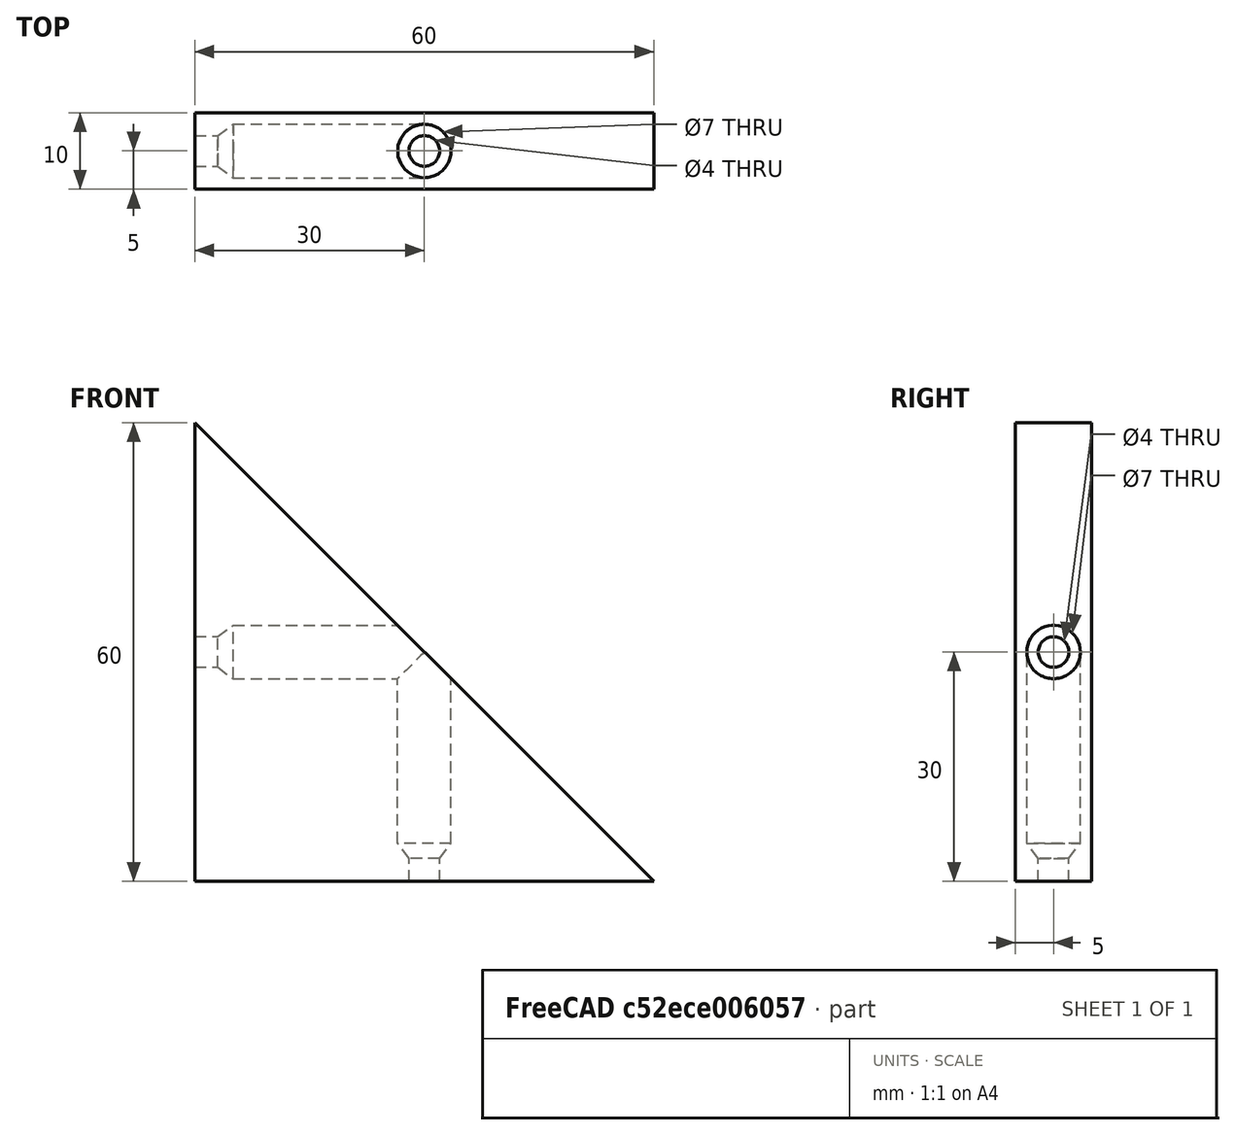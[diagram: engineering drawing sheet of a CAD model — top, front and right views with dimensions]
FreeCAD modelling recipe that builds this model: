
FCSTD DOCUMENT  (FreeCAD 0.16R6703 (Git))
Label: Escuadra Trasera
License: All rights reserved
LicenseURL: http://en.wikipedia.org/wiki/All_rights_reserved
objects: Part::MultiFuse×3, Part::Cylinder×2, Part::Wedge×1, Part::Cone×1, Part::Cut×1
note: 8 computed .brp shape members not serialized (recipe doc carries the construction recipe); baked Part::Feature solids carry a one-line shape summary decoded from their .brp

FEATURE [Part::Wedge] Wedge
  Placement = pos=(0,0,0) rot=(0,0,-1;1.5708rad)
  X2max = 10
  X2min = 0
  Xmax = 10
  Xmin = 0
  Ymax = 60
  Ymin = 0
  Z2max = 0
  Z2min = 0
  Zmax = 60
  Zmin = 0
FEATURE [Part::Cylinder] Cylinder
  Angle = 360
  Height = 10
  Placement = pos=(15,-5,0) rot=(0,0,1;0rad)
  Radius = 2
FEATURE [Part::Cylinder] Cylinder001
  Angle = 360
  Height = 34
  Placement = pos=(15,-5,5) rot=(0,0,1;0rad)
  Radius = 3.5
FEATURE [Part::Cone] Cone
  Angle = 360
  Height = 2
  Placement = pos=(15,-5,3) rot=(0,0,1;0rad)
  Radius1 = 2
  Radius2 = 3.5
FEATURE [Part::MultiFuse] Fusion
  Placement = pos=(0,0,45) rot=(0,1,0;1.5708rad)
  Shapes = -> [Cylinder,Cylinder001,Cone]
FEATURE [Part::MultiFuse] Fusion001
  Placement = pos=(15,0,0) rot=(0,0,1;0rad)
  Shapes = -> [Cylinder,Cylinder001,Cone]
FEATURE [Part::MultiFuse] Fusion002
  Shapes = -> [Fusion,Fusion001]
FEATURE [Part::Cut] Cut
  Base = -> Wedge
  Tool = -> Fusion002
